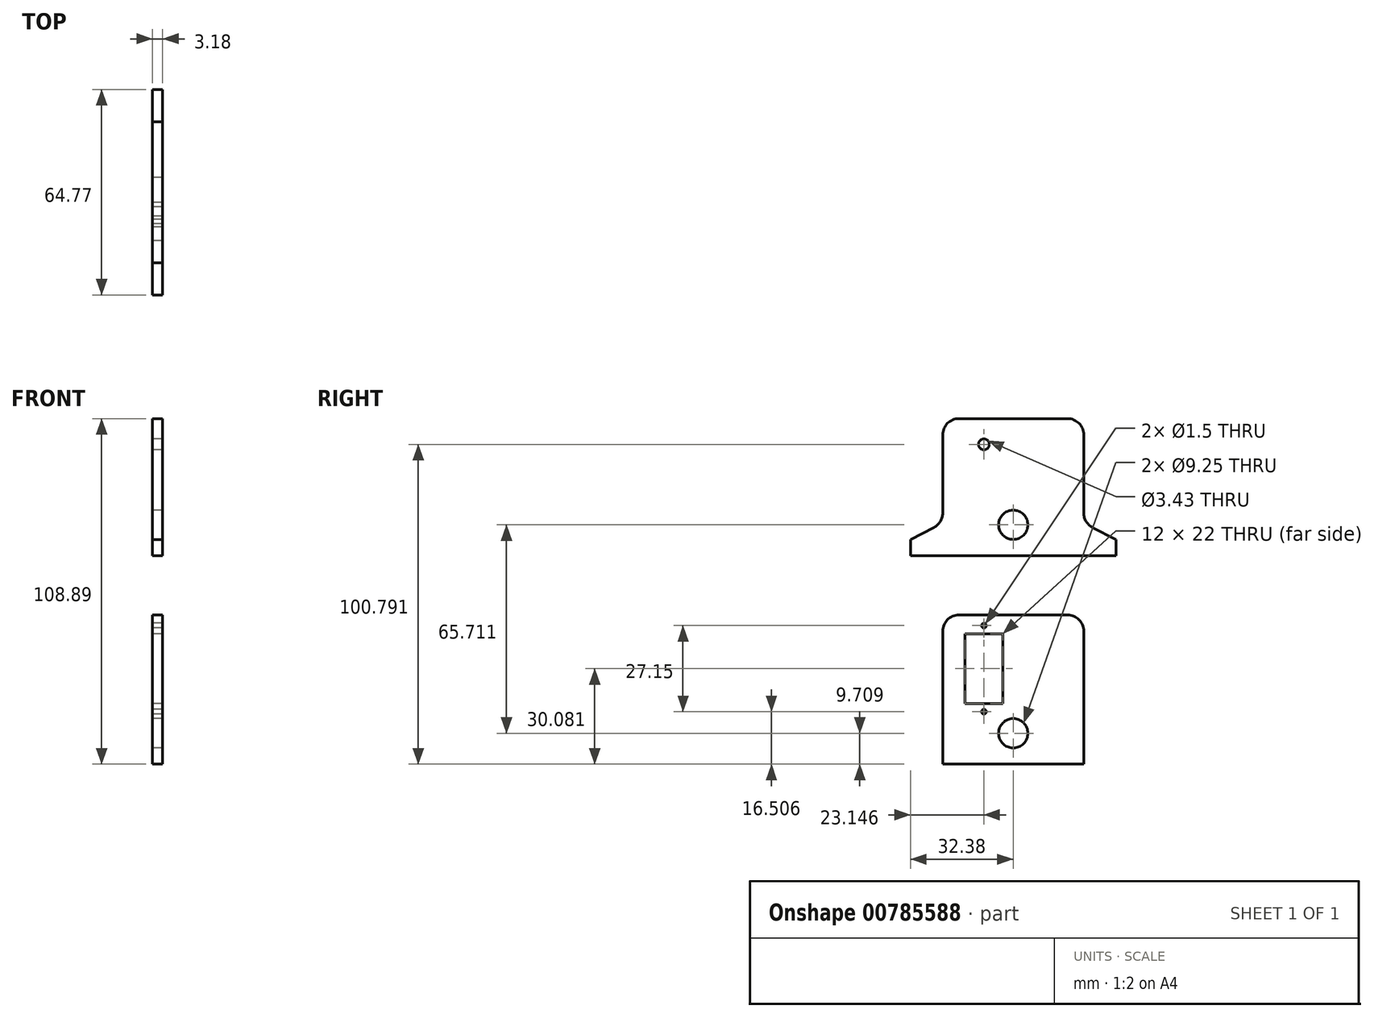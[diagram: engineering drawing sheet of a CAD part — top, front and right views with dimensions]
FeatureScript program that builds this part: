
annotation { "Feature Type Name" : "Feature", "Feature Type Description" : "" }
export const myFeature = defineFeature(function(context is Context, id is Id, definition is map)
    precondition{}
    {
        {
            var Q0;
            Q0=qCreatedBy(makeId("Right.planeOp"),FACE);
            var sketch = newSketch(context, id + "F0", { "sketchPlane" : qUnion([Q0])});
            skLineSegment(sketch, "E0.top", {"start": v(-72.3, 2.55) * mm, "end": v(-27.85, 2.55) * mm});
            skLineSegment(sketch, "E0.left", {"start": v(-72.3, -44.44) * mm, "end": v(-72.3, 2.55) * mm});
            skLineSegment(sketch, "E0.right", {"start": v(-27.85, -41.26) * mm, "end": v(-27.85, 2.55) * mm});
            skLineSegment(sketch, "E1.bottom", {"start": v(-53.31, -25.36) * mm, "end": v(-65.31, -25.36) * mm});
            skLineSegment(sketch, "E1.top", {"start": v(-53.31, -3.36) * mm, "end": v(-65.31, -3.36) * mm});
            skLineSegment(sketch, "E1.left", {"start": v(-53.31, -25.36) * mm, "end": v(-53.31, -3.36) * mm});
            skLineSegment(sketch, "E1.right", {"start": v(-65.31, -25.36) * mm, "end": v(-65.31, -3.36) * mm});
            skLineSegment(sketch, "E2", {"start": v(-65.31, -3.36) * mm, "end": v(-65.31, 1.8) * mm});
            skLineSegment(sketch, "E3", {"start": v(-65.31, 1.8) * mm, "end": v(-53.31, 1.8) * mm});
            skLineSegment(sketch, "E4", {"start": v(-53.31, 1.8) * mm, "end": v(-53.31, -3.36) * mm});
            skLineSegment(sketch, "E5", {"start": v(-53.31, -25.36) * mm, "end": v(-53.31, -30.5) * mm});
            skLineSegment(sketch, "E6", {"start": v(-53.31, -30.5) * mm, "end": v(-65.31, -30.5) * mm});
            skLineSegment(sketch, "E7", {"start": v(-65.31, -30.5) * mm, "end": v(-65.31, -25.36) * mm});
            skCircle(sketch, "E8", {"center": v(-59.31, -9.36) * mm, "radius": 6 * mm});
            skPoint(sketch, "E8.centerSnap0", {"position": v(-59.31, -3.36) * mm});
            skArc(sketch, "E9", {"start": v(-61.62, -14.9) * mm, "mid": v(-59.31, -18.36) * mm, "end": v(-57, -14.9) * mm});
            skCircle(sketch, "E10", {"center": v(-59.31, -0.78) * mm, "radius": 0.75 * mm});
            skPoint(sketch, "E10.centerSnap0", {"position": v(-65.31, -0.78) * mm});
            skPoint(sketch, "E10.centerSnap1", {"position": v(-59.31, 1.8) * mm});
            skCircle(sketch, "E11", {"center": v(-59.31, -27.93) * mm, "radius": 0.75 * mm});
            skPoint(sketch, "E11.centerSnap0", {"position": v(-59.31, -25.36) * mm});
            skPoint(sketch, "E11.centerSnap1", {"position": v(-65.31, -27.93) * mm});
            skCircle(sketch, "E12", {"center": v(-59.31, -9.36) * mm, "radius": 2.25 * mm});
            skPoint(sketch, "E13", {"position": v(-50.08, 2.55) * mm});
            skCircle(sketch, "E14", {"center": v(-50.08, -34.73) * mm, "radius": 4.62 * mm});
            skLineSegment(sketch, "E15", {"start": v(-50.08, 2.55) * mm, "end": v(-50.08, -44.44) * mm, "construction": true});
            skLineSegment(sketch, "E16", {"start": v(-59.31, -9.36) * mm, "end": v(-50.08, -34.73) * mm, "construction": true});
            skLineSegment(sketch, "E17.bottom", {"start": v(-72.3, 21.27) * mm, "end": v(-27.85, 21.27) * mm});
            skLineSegment(sketch, "E17.top", {"start": v(-61.38, 64.45) * mm, "end": v(-59.6, 64.45) * mm});
            skLineSegment(sketch, "E17.left", {"start": v(-72.3, 21.27) * mm, "end": v(-72.3, 64.45) * mm});
            skLineSegment(sketch, "E18.bottom", {"start": v(-53.31, 40.35) * mm, "end": v(-65.31, 40.35) * mm, "construction": true});
            skLineSegment(sketch, "E18.top", {"start": v(-53.31, 62.35) * mm, "end": v(-65.31, 62.35) * mm, "construction": true});
            skLineSegment(sketch, "E18.left", {"start": v(-53.31, 40.35) * mm, "end": v(-53.31, 62.35) * mm, "construction": true});
            skLineSegment(sketch, "E18.right", {"start": v(-65.31, 40.35) * mm, "end": v(-65.31, 62.35) * mm, "construction": true});
            skLineSegment(sketch, "E19", {"start": v(-65.31, 62.35) * mm, "end": v(-65.31, 67.5) * mm, "construction": true});
            skLineSegment(sketch, "E20", {"start": v(-65.31, 67.5) * mm, "end": v(-53.31, 67.5) * mm, "construction": true});
            skLineSegment(sketch, "E21", {"start": v(-53.31, 67.5) * mm, "end": v(-53.31, 62.35) * mm, "construction": true});
            skLineSegment(sketch, "E22", {"start": v(-53.31, 40.35) * mm, "end": v(-53.31, 35.2) * mm, "construction": true});
            skLineSegment(sketch, "E23", {"start": v(-53.31, 35.2) * mm, "end": v(-65.31, 35.2) * mm, "construction": true});
            skLineSegment(sketch, "E24", {"start": v(-65.31, 35.2) * mm, "end": v(-65.31, 40.35) * mm, "construction": true});
            skCircle(sketch, "E25", {"center": v(-59.31, 56.35) * mm, "radius": 6 * mm, "construction": true});
            skPoint(sketch, "E25.centerSnap0", {"position": v(-59.31, 62.35) * mm});
            skArc(sketch, "E26", {"start": v(-61.62, 50.81) * mm, "mid": v(-59.31, 47.35) * mm, "end": v(-57, 50.81) * mm, "construction": true});
            skCircle(sketch, "E27", {"center": v(-59.31, 64.93) * mm, "radius": 0.75 * mm, "construction": true});
            skPoint(sketch, "E27.centerSnap0", {"position": v(-65.31, 64.93) * mm});
            skPoint(sketch, "E27.centerSnap1", {"position": v(-59.31, 67.5) * mm});
            skCircle(sketch, "E28", {"center": v(-59.31, 37.78) * mm, "radius": 0.75 * mm, "construction": true});
            skPoint(sketch, "E28.centerSnap0", {"position": v(-59.31, 40.35) * mm});
            skPoint(sketch, "E28.centerSnap1", {"position": v(-65.31, 37.78) * mm});
            skCircle(sketch, "E29", {"center": v(-59.31, 56.35) * mm, "radius": 2.25 * mm, "construction": true});
            skPoint(sketch, "E30", {"position": v(-50.08, 64.45) * mm});
            skPoint(sketch, "E31", {"position": v(-50.08, 21.27) * mm});
            skCircle(sketch, "E32", {"center": v(-50.08, 30.98) * mm, "radius": 4.62 * mm});
            skLineSegment(sketch, "E33", {"start": v(-50.08, 64.45) * mm, "end": v(-50.08, 21.27) * mm, "construction": true});
            skLineSegment(sketch, "E34", {"start": v(-59.31, 56.35) * mm, "end": v(-50.08, 30.98) * mm, "construction": true});
            skCircle(sketch, "E35", {"center": v(-59.31, 56.35) * mm, "radius": 1.71 * mm});
            skPoint(sketch, "E36.visualSharp", {"position": v(-72.3, 64.45) * mm});
            skPoint(sketch, "E37.visualSharp", {"position": v(-54.52, 64.45) * mm});
            skLineSegment(sketch, "E38", {"start": v(-72.3, 64.45) * mm, "end": v(-27.85, 64.45) * mm});
            skLineSegment(sketch, "E39", {"start": v(-27.85, 64.45) * mm, "end": v(-27.85, 21.27) * mm});
            skLineSegment(sketch, "E40", {"start": v(-74.84, 21.27) * mm, "end": v(-77.38, 21.27) * mm});
            skLineSegment(sketch, "E41", {"start": v(-82.46, 21.27) * mm, "end": v(-82.46, 26.35) * mm});
            skLineSegment(sketch, "E42", {"start": v(-82.46, 26.35) * mm, "end": v(-72.3, 31.6) * mm});
            skLineSegment(sketch, "E43.trimOffspring", {"start": v(-72.3, 21.27) * mm, "end": v(-82.46, 21.27) * mm});
            skPoint(sketch, "E44.end.orphan", {"position": v(-79.92, 21.27) * mm});
            skPoint(sketch, "E45.start.orphan", {"position": v(-79.92, 24.45) * mm});
            skPoint(sketch, "E46.1.0.0.start.orphan", {"position": v(-77.38, 24.45) * mm});
            skPoint(sketch, "E47.trimOffspring.end.orphan", {"position": v(-72.3, 24.45) * mm});
            skPoint(sketch, "E47.trimOffspring.start.orphan", {"position": v(-74.84, 24.45) * mm});
            skLineSegment(sketch, "E48.MirrorCS", {"start": v(-17.7, 26.35) * mm, "end": v(-27.85, 31.6) * mm});
            skLineSegment(sketch, "E49.MirrorCS", {"start": v(-17.7, 21.27) * mm, "end": v(-17.7, 26.35) * mm});
            skLineSegment(sketch, "E50.MirrorCS", {"start": v(-27.85, 21.27) * mm, "end": v(-17.7, 21.27) * mm});
            skLineSegment(sketch, "E51", {"start": v(-72.3, -44.44) * mm, "end": v(-27.85, -44.44) * mm});
            skLineSegment(sketch, "E52", {"start": v(-27.85, -44.44) * mm, "end": v(-27.85, -41.26) * mm});
            skSolve(sketch);
        }
        {
            var Q0;
            Q0=makeQuery(id+"F0.imprint","IMPRINT",FACE,{"disambiguationData":[TD([[makeQuery(id+"F0.imprint","IMPRINT",EDGE,{"derivedFrom":sQuery(id+"F0.wireOp",EDGE,"E17.bottom")}),1.0]])]});
            var Q1;
            Q1=makeQuery(id+"F0.imprint","IMPRINT",FACE,{"disambiguationData":[TD([[makeQuery(id+"F0.imprint","IMPRINT",EDGE,{"derivedFrom":sQuery(id+"F0.wireOp",EDGE,"1f746809-ccef-4b12-823a-4d46f3119de00.MirrorC")}),1.0]])]});
            var Q2;
            Q2=makeQuery(id+"F0.imprint","IMPRINT",FACE,{"disambiguationData":[TD([[makeQuery(id+"F0.imprint","IMPRINT",EDGE,{"derivedFrom":sQuery(id+"F0.wireOp",EDGE,"E0.bottom")}),1.0]])]});
            var Q3;
            {var subQ0=sQuery(id+"F0.wireOp",EDGE,"E2");Q3=makeQuery(id+"F0.imprint","IMPRINT",FACE,{"disambiguationData":[TD([[makeQuery(id+"F0.imprint","IMPRINT",EDGE,{"derivedFrom":subQ0}),-1.0]])]});}
            var Q4;
            Q4=makeQuery(id+"F0.imprint","IMPRINT",FACE,{"disambiguationData":[TD([[makeQuery(id+"F0.imprint","IMPRINT",EDGE,{"derivedFrom":sQuery(id+"F0.wireOp",EDGE,"E1.bottom")}),1.0]])]});
            var Q5;
            Q5=makeQuery(id+"F0.imprint","IMPRINT",FACE,{"disambiguationData":[TD([[makeQuery(id+"F0.imprint","IMPRINT",EDGE,{"derivedFrom":sQuery(id+"F0.wireOp",EDGE,"1f746809-ccef-4b12-823a-4d46f3119de06.MirrorCS")}),-1.0]])]});
            var Q6;
            Q6=makeQuery(id+"F0.imprint","IMPRINT",FACE,{"disambiguationData":[TD([[makeQuery(id+"F0.imprint","IMPRINT",EDGE,{"derivedFrom":sQuery(id+"F0.wireOp",EDGE,"1f746809-ccef-4b12-823a-4d46f3119de06.MirrorCS")}),1.0]])]});
            var Q7;
            Q7=makeQuery(id+"F0.imprint","IMPRINT",FACE,{"disambiguationData":[TD([[makeQuery(id+"F0.imprint","IMPRINT",EDGE,{"derivedFrom":sQuery(id+"F0.wireOp",EDGE,"1f746809-ccef-4b12-823a-4d46f3119de07.MirrorCS")}),1.0]])]});
            var Q8;
            {var subQ0=sQuery(id+"F0.wireOp",EDGE,"E40");Q8=makeQuery(id+"F0.imprint","IMPRINT",FACE,{"disambiguationData":[TD([[makeQuery(id+"F0.imprint","IMPRINT",EDGE,{"derivedFrom":subQ0}),-1.0]])]});}
            var Q9;
            {var subQ0=sQuery(id+"F0.wireOp",EDGE,"8uHRKErG-xpJO-3P6K-E8NM-Eplvou1I3j8i");Q9=makeQuery(id+"F0.imprint","IMPRINT",FACE,{"disambiguationData":[TD([[makeQuery(id+"F0.imprint","IMPRINT",EDGE,{"derivedFrom":subQ0}),1.0]])]});}
            var Q10;
            {var subQ1=sQuery(id+"F0.wireOp",EDGE,"3a270411-9b2d-4279-b312-c21b0d60b1990.MirrorCS");Q10=makeQuery(id+"F0.imprint","IMPRINT",FACE,{"disambiguationData":[TD([[makeQuery(id+"F0.imprint","IMPRINT",EDGE,{"derivedFrom":subQ1}),1.0]])]});}
            var Q11;
            {var subQ15=sQuery(id+"F0.wireOp",EDGE,"E0.top");Q11=makeQuery(id+"F0.imprint","IMPRINT",FACE,{"disambiguationData":[TD([[makeQuery(id+"F0.imprint","IMPRINT",EDGE,{"derivedFrom":subQ15}),-1.0]])]});}
            var Q12;
            {var subQ0=sQuery(id+"F0.wireOp",EDGE,"f7504665-03c3-4bab-ba1b-32a0b06b7112.1.0.0");Q12=makeQuery(id+"F0.imprint","IMPRINT",FACE,{"disambiguationData":[TD([[makeQuery(id+"F0.imprint","IMPRINT",EDGE,{"derivedFrom":subQ0}),1.0]])]});}
            var Q13;
            {var subQ0=sQuery(id+"F0.wireOp",EDGE,"02fc8d48-d24e-4b29-a73e-621c5b1f1a92.0.3.0");Q13=makeQuery(id+"F0.imprint","IMPRINT",FACE,{"disambiguationData":[TD([[makeQuery(id+"F0.imprint","IMPRINT",EDGE,{"derivedFrom":subQ0}),1.0]])]});}
            var Q14;
            {var subQ0=sQuery(id+"F0.wireOp",EDGE,"6fac29db-3882-497f-8155-b8b778b409b2.0.5.0");Q14=makeQuery(id+"F0.imprint","IMPRINT",FACE,{"disambiguationData":[TD([[makeQuery(id+"F0.imprint","IMPRINT",EDGE,{"derivedFrom":subQ0}),1.0]])]});}
            var Q15;
            {var subQ0=sQuery(id+"F0.wireOp",EDGE,"6fac29db-3882-497f-8155-b8b778b409b2.0.7.0");Q15=makeQuery(id+"F0.imprint","IMPRINT",FACE,{"disambiguationData":[TD([[makeQuery(id+"F0.imprint","IMPRINT",EDGE,{"derivedFrom":subQ0}),1.0]])]});}
            var Q16;
            {var subQ0=sQuery(id+"F0.wireOp",EDGE,"6fac29db-3882-497f-8155-b8b778b409b2.0.9.0");Q16=makeQuery(id+"F0.imprint","IMPRINT",FACE,{"disambiguationData":[TD([[makeQuery(id+"F0.imprint","IMPRINT",EDGE,{"derivedFrom":subQ0}),1.0]])]});}
            var Q17;
            {var subQ0=sQuery(id+"F0.wireOp",EDGE,"6fac29db-3882-497f-8155-b8b778b409b2.0.11.0");Q17=makeQuery(id+"F0.imprint","IMPRINT",FACE,{"disambiguationData":[TD([[makeQuery(id+"F0.imprint","IMPRINT",EDGE,{"derivedFrom":subQ0}),1.0]])]});}
            var Q18;
            {var subQ0=sQuery(id+"F0.wireOp",EDGE,"6fac29db-3882-497f-8155-b8b778b409b2.0.13.0");Q18=makeQuery(id+"F0.imprint","IMPRINT",FACE,{"disambiguationData":[TD([[makeQuery(id+"F0.imprint","IMPRINT",EDGE,{"derivedFrom":subQ0}),1.0]])]});}
            var Q19;
            {var subQ0=sQuery(id+"F0.wireOp",EDGE,"6fac29db-3882-497f-8155-b8b778b409b2.0.15.0");Q19=makeQuery(id+"F0.imprint","IMPRINT",FACE,{"disambiguationData":[TD([[makeQuery(id+"F0.imprint","IMPRINT",EDGE,{"derivedFrom":subQ0}),1.0]])]});}
            var Q20;
            {var subQ4=sQuery(id+"F0.wireOp",EDGE,"E41");Q20=makeQuery(id+"F0.imprint","IMPRINT",FACE,{"disambiguationData":[TD([[makeQuery(id+"F0.imprint","IMPRINT",EDGE,{"derivedFrom":subQ4}),-1.0]])]});}
            var Q21;
            {var subQ2=sQuery(id+"F0.wireOp",EDGE,"E48.MirrorCS");Q21=makeQuery(id+"F0.imprint","IMPRINT",FACE,{"disambiguationData":[TD([[makeQuery(id+"F0.imprint","IMPRINT",EDGE,{"derivedFrom":subQ2}),1.0]])]});}
            extrude(context, id + "F1", {"entities" : qUnion([Q0, Q1, Q2, Q3, Q4, Q5, Q6, Q7, Q8, Q9, Q10, Q11, Q12, Q13, Q14, Q15, Q16, Q17, Q18, Q19, Q20, Q21]), "depth" : 3.17 * mm, "offsetDistance" : 25.4 * mm});
        }
        {
            var Q0;
            Q0=makeQuery(id+"F1.opExtrude","SWEPT_EDGE",EDGE,{"disambiguationData":[OSD([sQuery(id+"F0.wireOp",EDGE,"E17.left"),sQuery(id+"F0.wireOp",EDGE,"E38")])]});
            var Q1;
            Q1=makeQuery(id+"F1.opExtrude","SWEPT_EDGE",EDGE,{"disambiguationData":[OSD([sQuery(id+"F0.wireOp",EDGE,"E17.left"),sQuery(id+"F0.wireOp",EDGE,"E42")])]});
            var Q2;
            Q2=makeQuery(id+"F1.opExtrude","SWEPT_EDGE",EDGE,{"disambiguationData":[OSD([sQuery(id+"F0.wireOp",EDGE,"E38"),sQuery(id+"F0.wireOp",EDGE,"E39")])]});
            var Q3;
            Q3=makeQuery(id+"F1.opExtrude","SWEPT_EDGE",EDGE,{"disambiguationData":[OSD([sQuery(id+"F0.wireOp",EDGE,"E0.top"),sQuery(id+"F0.wireOp",EDGE,"E0.left")])]});
            var Q4;
            Q4=makeQuery(id+"F1.opExtrude","SWEPT_EDGE",EDGE,{"disambiguationData":[OSD([sQuery(id+"F0.wireOp",EDGE,"E0.top"),sQuery(id+"F0.wireOp",EDGE,"E0.right")])]});
            var Q5;
            Q5=makeQuery(id+"F1.opExtrude","SWEPT_EDGE",EDGE,{"disambiguationData":[OSD([sQuery(id+"F0.wireOp",EDGE,"E39"),sQuery(id+"F0.wireOp",EDGE,"3a270411-9b2d-4279-b312-c21b0d60b1990.MirrorCS")])]});
            fillet(context, id + "F2", {"entities" : qUnion([Q0, Q1, Q2, Q3, Q4, Q5]), "radius" : 5.08 * mm, "tangentPropagation" : true, "allowEdgeOverflow" : false});
        }
    });
